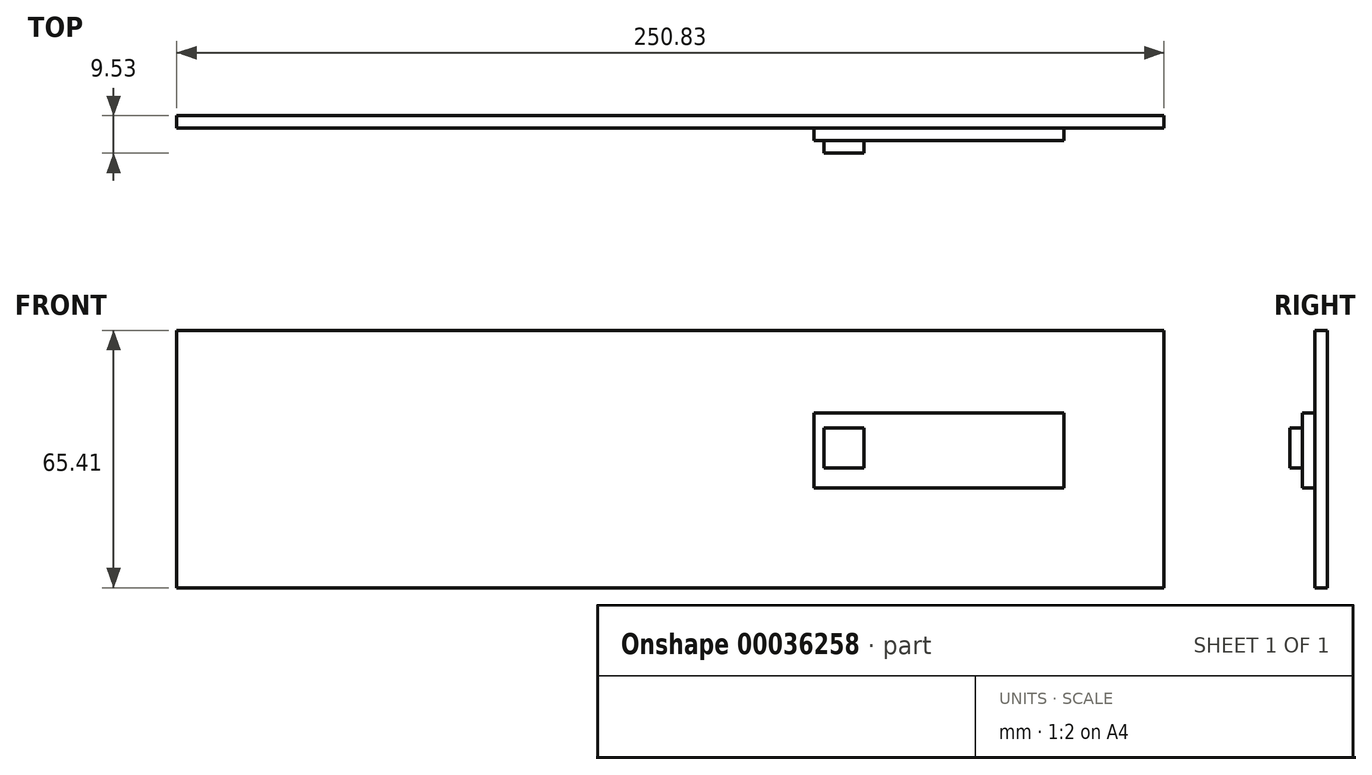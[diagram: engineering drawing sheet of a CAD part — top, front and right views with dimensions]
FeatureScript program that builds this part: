
annotation { "Feature Type Name" : "Feature", "Feature Type Description" : "" }
export const myFeature = defineFeature(function(context is Context, id is Id, definition is map)
    precondition{}
    {
        {
            var Q0;
            Q0=qCreatedBy(makeId("Front.planeOp"),FACE);
            var sketch = newSketch(context, id + "F0", { "sketchPlane" : qUnion([Q0])});
            skLineSegment(sketch, "E0.bottom", {"start": v(0, 0) * mm, "end": v(250.83, 0) * mm});
            skLineSegment(sketch, "E0.top", {"start": v(0, 65.4) * mm, "end": v(250.83, 65.4) * mm});
            skLineSegment(sketch, "E0.left", {"start": v(0, 0) * mm, "end": v(0, 65.4) * mm});
            skLineSegment(sketch, "E0.right", {"start": v(250.83, 0) * mm, "end": v(250.83, 65.4) * mm});
            skSolve(sketch);
        }
        {
            var Q0;
            Q0=qSketchRegion(id+"F0",true);
            extrude(context, id + "F1", {"entities" : qUnion([Q0]), "depth" : 3.17 * mm});
        }
        {
            var Q0;
            Q0=makeQuery(id+"F1.opExtrude","CAP_FACE",FACE,{"disambiguationData":[OSD([sQuery(id+"F0.wireOp",EDGE,"E0.bottom"),sQuery(id+"F0.wireOp",EDGE,"E0.top"),sQuery(id+"F0.wireOp",EDGE,"E0.left"),sQuery(id+"F0.wireOp",EDGE,"E0.right")])],"isStart":false});
            var sketch = newSketch(context, id + "F2", { "sketchPlane" : qUnion([Q0])});
            skLineSegment(sketch, "E1.bottom", {"start": v(161.93, 44.45) * mm, "end": v(225.43, 44.45) * mm});
            skLineSegment(sketch, "E1.top", {"start": v(161.93, 25.4) * mm, "end": v(225.43, 25.4) * mm});
            skLineSegment(sketch, "E1.left", {"start": v(161.93, 44.45) * mm, "end": v(161.93, 25.4) * mm});
            skLineSegment(sketch, "E1.right", {"start": v(225.43, 44.45) * mm, "end": v(225.43, 25.4) * mm});
            skSolve(sketch);
        }
        {
            var Q0;
            Q0=qSketchRegion(id+"F2",true);
            extrude(context, id + "F3", {"entities" : qUnion([Q0]), "operationType" : NewBodyOperationType.ADD, "depth" : 3.17 * mm});
        }
        {
            var Q0;
            Q0=makeQuery(id+"F3.opExtrude","CAP_FACE",FACE,{"disambiguationData":[OSD([sQuery(id+"F2.wireOp",EDGE,"E1.bottom"),sQuery(id+"F2.wireOp",EDGE,"E1.top"),sQuery(id+"F2.wireOp",EDGE,"E1.left"),sQuery(id+"F2.wireOp",EDGE,"E1.right")])],"isStart":false});
            var sketch = newSketch(context, id + "F4", { "sketchPlane" : qUnion([Q0])});
            skLineSegment(sketch, "E2.bottom", {"start": v(164.47, 40.64) * mm, "end": v(174.63, 40.64) * mm});
            skLineSegment(sketch, "E2.top", {"start": v(164.47, 30.48) * mm, "end": v(174.63, 30.48) * mm});
            skLineSegment(sketch, "E2.left", {"start": v(164.47, 40.64) * mm, "end": v(164.47, 30.48) * mm});
            skLineSegment(sketch, "E2.right", {"start": v(174.63, 40.64) * mm, "end": v(174.63, 30.48) * mm});
            skLineSegment(sketch, "E3.direction1", {"start": v(174.63, 30.48) * mm, "end": v(190.5, 30.48) * mm, "construction": true});
            skLineSegment(sketch, "E3.direction2", {"start": v(174.63, 30.48) * mm, "end": v(174.63, 14.6) * mm, "construction": true});
            skSolve(sketch);
        }
        {
            var Q0;
            Q0=qSketchRegion(id+"F4",true);
            extrude(context, id + "F5", {"entities" : qUnion([Q0]), "operationType" : NewBodyOperationType.ADD, "depth" : 3.17 * mm});
        }
    });
